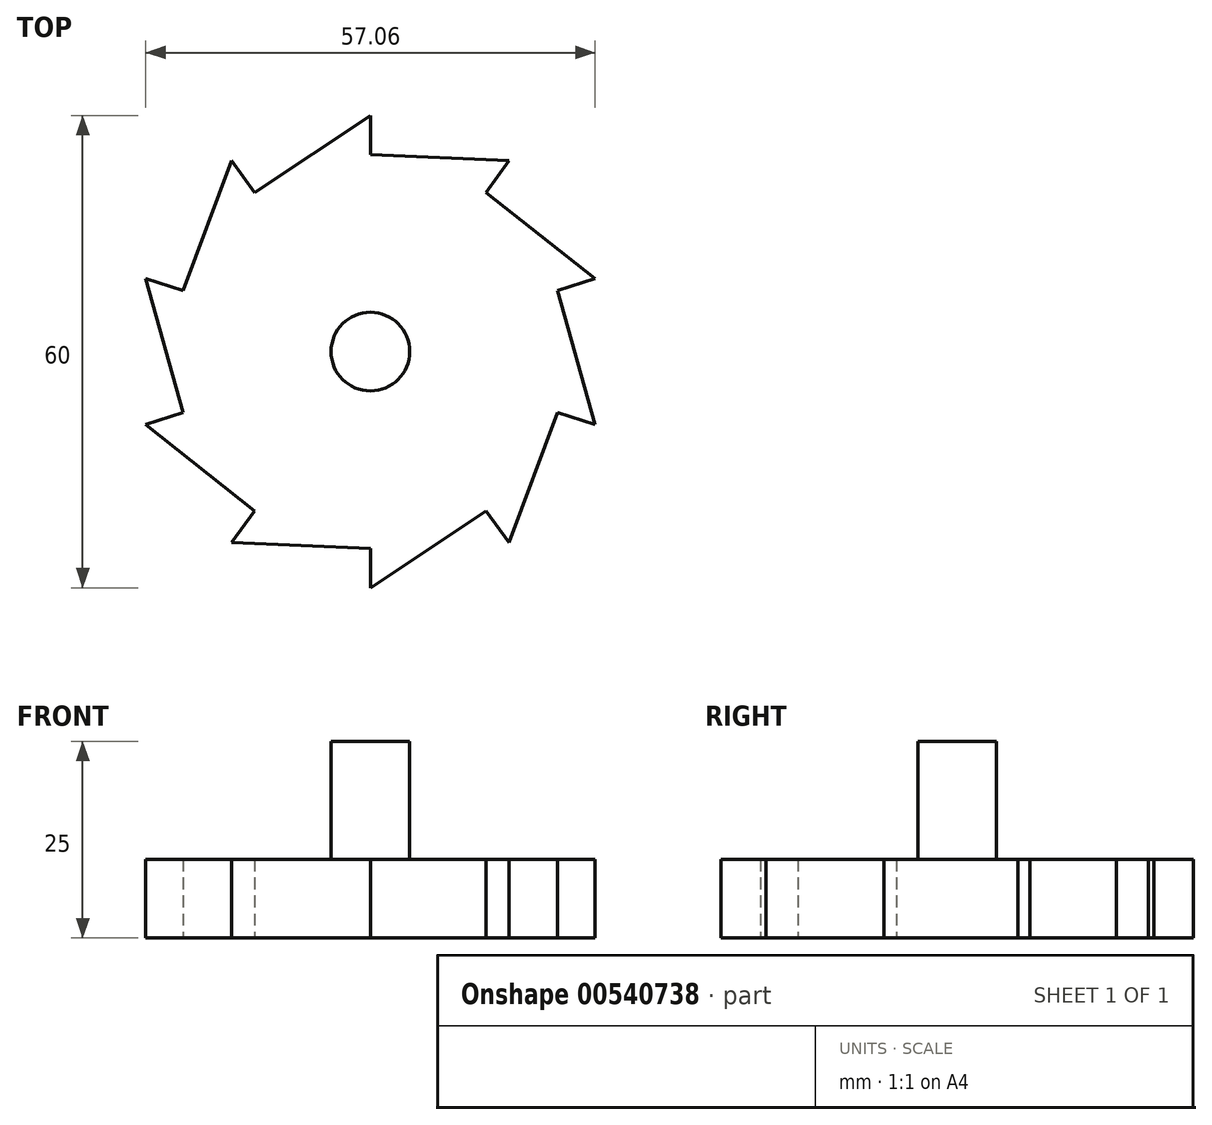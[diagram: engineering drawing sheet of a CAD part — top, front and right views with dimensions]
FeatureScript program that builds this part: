
annotation { "Feature Type Name" : "Feature", "Feature Type Description" : "" }
export const myFeature = defineFeature(function(context is Context, id is Id, definition is map)
    precondition{}
    {
        {
            var Q0;
            Q0=qCreatedBy(makeId("Top.planeOp"),FACE);
            var sketch = newSketch(context, id + "F0", { "sketchPlane" : qUnion([Q0])});
            skLineSegment(sketch, "E0", {"start": v(0, 30) * mm, "end": v(0, 25) * mm});
            skLineSegment(sketch, "E1.1.0", {"start": v(-17.63, 24.27) * mm, "end": v(-14.7, 20.23) * mm});
            skLineSegment(sketch, "E1.2.0", {"start": v(-28.53, 9.27) * mm, "end": v(-23.78, 7.73) * mm});
            skPoint(sketch, "E1.center", {"position": v(0, 0) * mm});
            skLineSegment(sketch, "E2.2.3.0", {"start": v(-28.53, -9.27) * mm, "end": v(-23.78, -7.73) * mm});
            skLineSegment(sketch, "E2.2.4.0", {"start": v(-17.63, -24.27) * mm, "end": v(-14.7, -20.23) * mm});
            skLineSegment(sketch, "E2.2.5.0", {"start": v(0, -30) * mm, "end": v(0, -25) * mm});
            skLineSegment(sketch, "E2.2.6.0", {"start": v(17.63, -24.27) * mm, "end": v(14.7, -20.23) * mm});
            skLineSegment(sketch, "E2.2.7.0", {"start": v(28.53, -9.27) * mm, "end": v(23.78, -7.73) * mm});
            skLineSegment(sketch, "E2.2.8.0", {"start": v(28.53, 9.27) * mm, "end": v(23.78, 7.73) * mm});
            skLineSegment(sketch, "E2.2.9.0", {"start": v(17.63, 24.27) * mm, "end": v(14.7, 20.23) * mm});
            skLineSegment(sketch, "E3", {"start": v(0, 25) * mm, "end": v(17.63, 24.27) * mm});
            skLineSegment(sketch, "E4", {"start": v(14.7, 20.23) * mm, "end": v(28.53, 9.27) * mm});
            skLineSegment(sketch, "E5", {"start": v(23.78, 7.73) * mm, "end": v(28.53, -9.27) * mm});
            skLineSegment(sketch, "E6", {"start": v(23.78, -7.73) * mm, "end": v(17.63, -24.27) * mm});
            skLineSegment(sketch, "E7", {"start": v(14.7, -20.23) * mm, "end": v(0, -30) * mm});
            skLineSegment(sketch, "E8", {"start": v(0, -25) * mm, "end": v(-17.63, -24.27) * mm});
            skLineSegment(sketch, "E9", {"start": v(-14.7, -20.23) * mm, "end": v(-28.53, -9.27) * mm});
            skLineSegment(sketch, "E10", {"start": v(-23.78, -7.73) * mm, "end": v(-28.53, 9.27) * mm});
            skLineSegment(sketch, "E11", {"start": v(-23.78, 7.73) * mm, "end": v(-17.63, 24.27) * mm});
            skLineSegment(sketch, "E12", {"start": v(-14.7, 20.23) * mm, "end": v(0, 30) * mm});
            skSolve(sketch);
        }
        {
            var Q0;
            Q0 = qSketchRegion(id + "F0", true);
            extrude(context, id + "F1", {"entities" : qUnion([Q0]), "depth" : 10 * mm, "offsetDistance" : 25 * mm});
        }
        {
            var Q0;
            Q0=qCreatedBy(makeId("Top.planeOp"),FACE);
            var sketch = newSketch(context, id + "F2", { "sketchPlane" : qUnion([Q0])});
            skCircle(sketch, "E13", {"center": v(0, 0) * mm, "radius": 5 * mm});
            skSolve(sketch);
        }
        {
            var Q0;
            Q0 = qSketchRegion(id + "F2", true);
            extrude(context, id + "F3", {"entities" : qUnion([Q0]), "operationType" : NewBodyOperationType.ADD, "depth" : 25 * mm, "offsetDistance" : 25 * mm});
        }
        {
            var Q0;
            Q0=qCreatedBy(makeId("Top.planeOp"),FACE);
            var sketch = newSketch(context, id + "F4", { "sketchPlane" : qUnion([Q0])});
            skCircle(sketch, "E14", {"center": v(0, 0) * mm, "radius": 5 * mm});
            skSolve(sketch);
        }
        {
            var Q0;
            Q0 = qSketchRegion(id + "F4", true);
            extrude(context, id + "F5", {"entities" : qUnion([Q0]), "operationType" : NewBodyOperationType.ADD, "depth" : 10 * mm, "offsetDistance" : 25 * mm});
        }
    });
